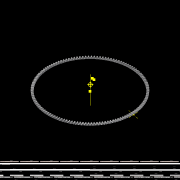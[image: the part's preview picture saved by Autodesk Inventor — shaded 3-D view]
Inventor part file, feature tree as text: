
AUTODESK INVENTOR PART (.ipt)
format: ipt  version: 2017 (Build 210142000, 142)  size: 1,784,832 bytes
history: native  units: mm
features: other x24, sketch x4, loft x2, pattern_circular x2, extrude x1
ambient origin geometry x6: Origin, XZ Plane, X Axis, Y Axis, Z Axis, Center Point
bodies: Solid1 (feature_tree)
feature tree (33):
  other  "Top Point"
  other  "Mesh Plane2"
  other  "Teeth Body"
  other  "Start Point"
  other  "Tooth Plane"
  other  "Start Sketch"
  other  "End Point"
  other  "3D Sketch Right"
  other  "End Plane Right"
  loft  "Loft Right"
  pattern_circular  "Circular Pattern Right"  Angle=90.0deg  [1 undecoded]
  other  "3D Sketch Left"
  other  "End Plane Left"
  loft  "Loft Left"
  pattern_circular  "Circular Pattern Left"  [2 undecoded]
  other  "Fix Body"
  sketch  "Sketch8"  dims[d2=325.711267mm]
  extrude  "Extrusion1"  Depth=10.0mm
  sketch  "Sketch10"  dims[d4=16.527263mm d5=90.0deg d7=478.580124mm d8=454.184503mm d9=1239.94227mm d11=7.8994mm d12=455.960761mm d15=432.718163mm d16=1181.338282mm d17=0.0mm d18=90.0deg d19=0.0mm d20=90.0deg d21=1280.0mm d22=360.0deg d26=314.208686mm d27=0.919419mm d28=325.12mm d29=-14.541409mm d30=455.960761mm d31=432.718163mm d32=1181.338282mm d35=0.0mm d37=0.0mm d39=0.0mm d40=90.0deg d41=1280.0mm d42=360.0deg d46=90.0deg d47=90.0deg d48=0.0mm d49=0.0mm d50=90.0deg d51=0.245437mm d52=0.0mm d53=0.0mm d54=0.0mm d56=18.102912mm d57=1400.887588mm d58=1392.952628mm d59=1334.676764mm d60=1327.116838mm d61=1334.676764mm d62=1327.116838mm d63=90.0deg d64=90.0deg d65=314.208686mm d66=31.5mm d67=325.12mm d68=-14.541409mm d69=0.919419mm d70=432.718163mm d71=1181.338282mm d72=455.960761mm d73=1327.116838mm d74=1334.676764mm d75=0.0mm d76=90.0deg d77=0.0mm d78=90.0deg d79=0.0mm d80=90.0deg d81=1280.0mm d82=360.0deg d84=10.0mm d85=20.0mm d86=20.0mm d87=10.0mm d88=0.0mm d89=0.0mm d90=25.4mm d91=0.0mm d92=309.2958mm]
  other  "Mesh Plane"
  other  "Top Plane"
  other  "Teeth Body Sketch"
  other  "End Plane"
  other  "End Sketch"
  other  "Helical Curve Left"
  other  "End Sketch Left"
  other  "Body Sketch"
  sketch  "Sketch6"  dims[d0=325.12mm d1=324.41048mm]
  other  "Srf1"
  other  "Helical Curve Right"
  other  "End Sketch Right"
  sketch  "Sketch9"  dims[d3=7.62mm]
  other  "Pitch Diameter"
note: 3 required parameter values undecoded (feature->parameter linkage not recoverable at this tier; creation-order binding heuristic only, values carry confidence <= 0.55)
